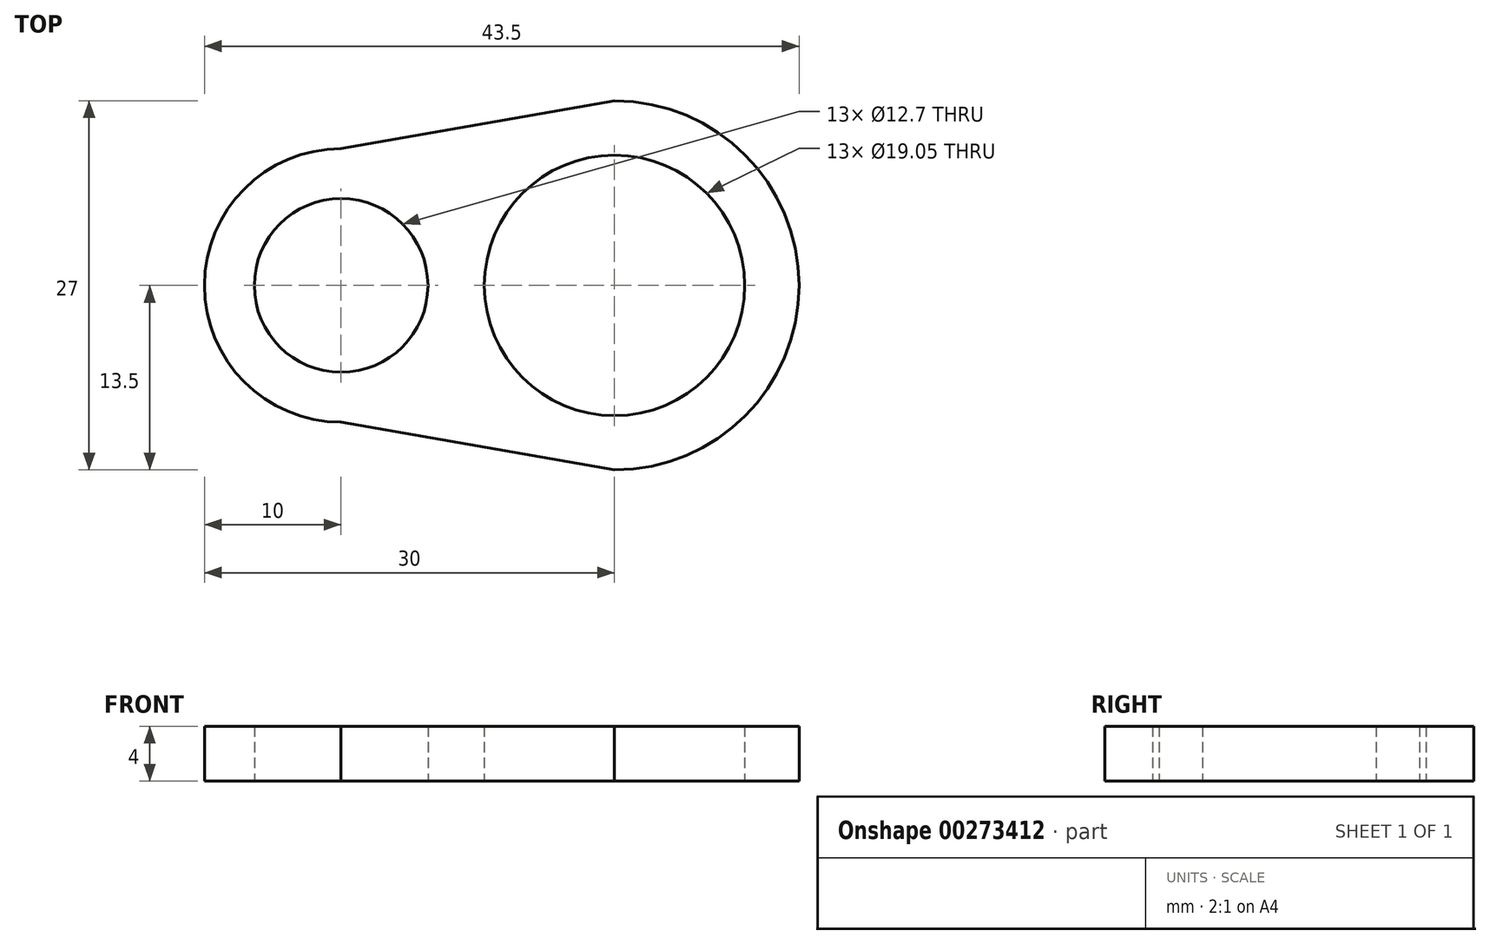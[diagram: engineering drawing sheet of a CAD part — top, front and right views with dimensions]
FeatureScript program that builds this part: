
annotation { "Feature Type Name" : "Feature", "Feature Type Description" : "" }
export const myFeature = defineFeature(function(context is Context, id is Id, definition is map)
    precondition{}
    {
        {
            var Q0;
            Q0=qCreatedBy(makeId("Top.planeOp"),FACE);
            var sketch = newSketch(context, id + "F0", { "sketchPlane" : qUnion([Q0])});
            skCircle(sketch, "E0", {"center": v(0, 0) * mm, "radius": 6.35 * mm});
            skCircle(sketch, "E1", {"center": v(20, 0) * mm, "radius": 9.53 * mm});
            skArc(sketch, "E2", {"start": v(0, 10) * mm, "mid": v(-10, 0) * mm, "end": v(0, -10) * mm});
            skArc(sketch, "E3", {"start": v(20, -13.5) * mm, "mid": v(33.5, 0) * mm, "end": v(20, 13.5) * mm});
            skLineSegment(sketch, "E4", {"start": v(0, -10) * mm, "end": v(20, -13.5) * mm});
            skLineSegment(sketch, "E5.MirrorCS", {"start": v(0, 10) * mm, "end": v(20, 13.5) * mm});
            skSolve(sketch);
        }
        {
            var Q0;
            Q0 = qSketchRegion(id + "F0", true);
            extrude(context, id + "F1", {"entities" : qUnion([Q0]), "depth" : 4 * mm});
        }
    });
